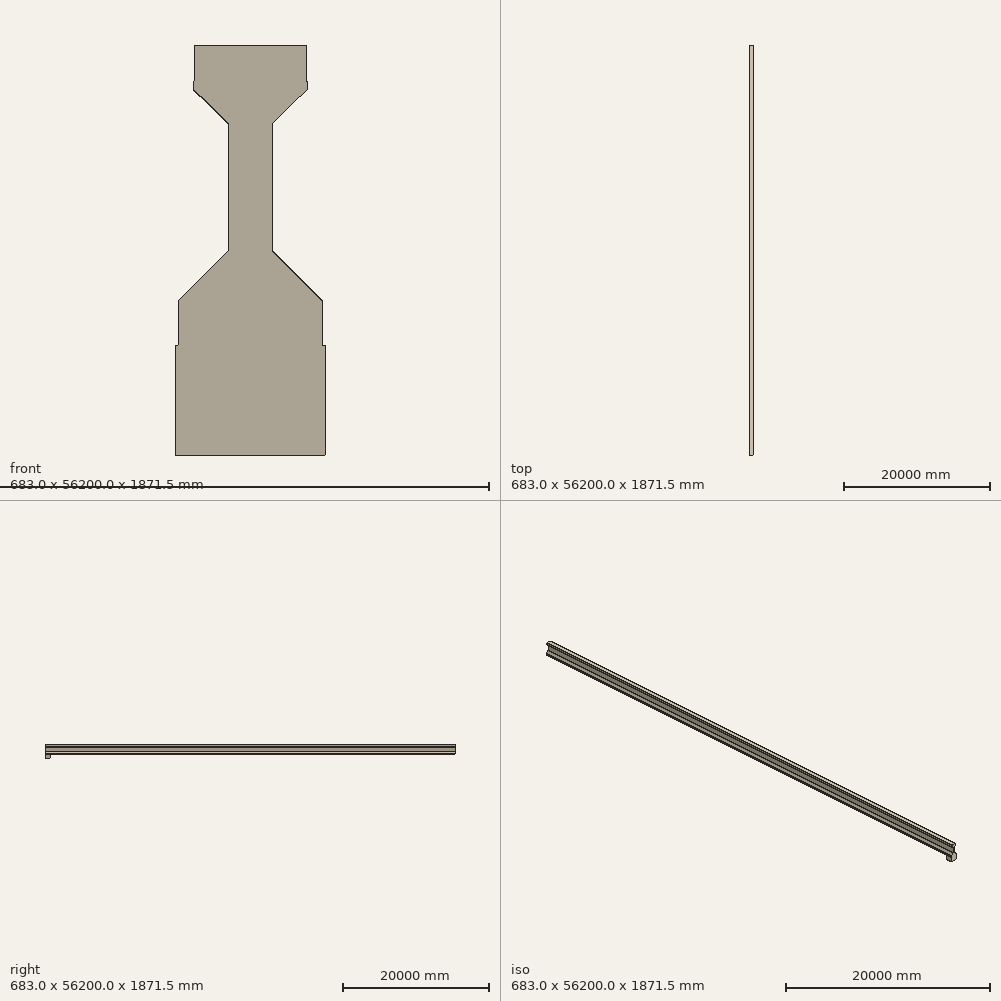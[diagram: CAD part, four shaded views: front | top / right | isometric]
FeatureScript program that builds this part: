
annotation { "Feature Type Name" : "Feature", "Feature Type Description" : "" }
export const myFeature = defineFeature(function(context is Context, id is Id, definition is map)
    precondition{}
    {
        {
            var Q0;
            Q0=qCreatedBy(makeId("Front.planeOp"),FACE);
            var sketch = newSketch(context, id + "F0", { "sketchPlane" : qUnion([Q0])});
            skLineSegment(sketch, "E0", {"start": v(0, 759.62) * mm, "end": v(-254, 759.62) * mm});
            skLineSegment(sketch, "E1", {"start": v(-254, 759.62) * mm, "end": v(-258.84, 556.48) * mm});
            skLineSegment(sketch, "E2", {"start": v(-258.84, 556.48) * mm, "end": v(-101.6, 404.08) * mm});
            skLineSegment(sketch, "E3", {"start": v(-101.6, 404.08) * mm, "end": v(-101.6, -180.12) * mm});
            skLineSegment(sketch, "E4", {"start": v(-101.6, -180.12) * mm, "end": v(-330.2, -408.72) * mm});
            skLineSegment(sketch, "E5", {"start": v(-330.2, -408.72) * mm, "end": v(-330.2, -611.92) * mm});
            skLineSegment(sketch, "E6", {"start": v(-330.2, -611.92) * mm, "end": v(0, -611.92) * mm});
            skLineSegment(sketch, "E7.MirrorCS", {"start": v(0, 759.62) * mm, "end": v(254, 759.62) * mm});
            skLineSegment(sketch, "E8.MirrorCS", {"start": v(254, 759.62) * mm, "end": v(258.84, 556.48) * mm});
            skLineSegment(sketch, "E9.MirrorCS", {"start": v(258.84, 556.48) * mm, "end": v(101.6, 404.08) * mm});
            skLineSegment(sketch, "E10.MirrorCS", {"start": v(101.6, 404.08) * mm, "end": v(101.6, -180.12) * mm});
            skLineSegment(sketch, "E11.MirrorCS", {"start": v(101.6, -180.12) * mm, "end": v(330.2, -408.72) * mm});
            skLineSegment(sketch, "E12.MirrorCS", {"start": v(330.2, -408.72) * mm, "end": v(330.2, -611.92) * mm});
            skLineSegment(sketch, "E13.MirrorCS", {"start": v(330.2, -611.92) * mm, "end": v(0, -611.92) * mm});
            skSolve(sketch);
        }
        {
            var Q0;
            Q0=makeQuery(id+"F0.imprint","IMPRINT",FACE,{"disambiguationData":[TD([[makeQuery(id+"F0.imprint","IMPRINT",EDGE,{"derivedFrom":sQuery(id+"F0.wireOp",EDGE,"E0")}),1.0]])]});
            extrude(context, id + "F1", {"entities" : qUnion([Q0]), "depth" : 56200 * mm});
        }
        {
            var Q0;
            Q0=makeQuery(id+"F1.opExtrude","SWEPT_FACE",FACE,{"disambiguationData":[OSD([sQuery(id+"F0.wireOp",EDGE,"E0"),sQuery(id+"F0.wireOp",EDGE,"E7.MirrorCS")])]});
            var sketch = newSketch(context, id + "F2", { "sketchPlane" : qUnion([Q0])});
            skLineSegment(sketch, "E14", {"start": v(-254, -56200) * mm, "end": v(0, -56200) * mm});
            skLineSegment(sketch, "E15", {"start": v(0, -56200) * mm, "end": v(0, -53450) * mm});
            skLineSegment(sketch, "E16", {"start": v(0, -56200) * mm, "end": v(254, -56200) * mm});
            skSolve(sketch);
        }
        {
            var Q0;
            Q0=makeQuery(id+"F1.opExtrude","SWEPT_FACE",FACE,{"disambiguationData":[OSD([sQuery(id+"F0.wireOp",EDGE,"E6"),sQuery(id+"F0.wireOp",EDGE,"E13.MirrorCS")])]});
            var sketch = newSketch(context, id + "F3", { "sketchPlane" : qUnion([Q0])});
            skLineSegment(sketch, "E17.bottom", {"start": v(341.5, 56200) * mm, "end": v(-341.5, 56200) * mm});
            skLineSegment(sketch, "E17.top", {"start": v(341.5, 55517) * mm, "end": v(-341.5, 55517) * mm});
            skLineSegment(sketch, "E17.left", {"start": v(341.5, 56200) * mm, "end": v(341.5, 55517) * mm});
            skLineSegment(sketch, "E17.right", {"start": v(-341.5, 56200) * mm, "end": v(-341.5, 55517) * mm});
            skPoint(sketch, "E17.middle", {"position": v(0, 55858.5) * mm});
            skPoint(sketch, "E17.middle.positionSnap0", {"position": v(0, 56200) * mm});
            skPoint(sketch, "E17.centerSnap0", {"position": v(0, 56200) * mm});
            skSolve(sketch);
        }
        {
            var Q0;
            {var subQ0=sQuery(id+"F3.wireOp",EDGE,"E17.bottom");var subQ1=makeQuery(id+"F1.opExtrude","SWEPT_EDGE",EDGE,{"disambiguationData":[OSD([sQuery(id+"F0.wireOp",EDGE,"E5"),sQuery(id+"F0.wireOp",EDGE,"E6")])]});var subQ2=makeQuery(id+"F3.imprint","INTERSECT",VERTEX,{"derivedFrom":[subQ1,subQ0]});var subQ3=makeQuery(id+"F1.opExtrude","SWEPT_EDGE",EDGE,{"disambiguationData":[OSD([sQuery(id+"F0.wireOp",EDGE,"E12.MirrorCS"),sQuery(id+"F0.wireOp",EDGE,"E13.MirrorCS")])]});var subQ4=makeQuery(id+"F3.imprint","INTERSECT",VERTEX,{"derivedFrom":[subQ3,subQ0]});Q0=makeQuery(id+"F3.imprint","IMPRINT",FACE,{"disambiguationData":[TD([[makeQuery(id+"F3.imprint","IMPRINT",EDGE,{"disambiguationData":[TD([[subQ2,-1.0],[subQ4,1.0]])],"derivedFrom":subQ0}),-1.0]])]});}
            extrude(context, id + "F4", {"entities" : qUnion([Q0]), "depth" : 500 * mm});
        }
        {
            var Q0;
            {var subQ3=sQuery(id+"F3.wireOp",EDGE,"E17.left");Q0=makeQuery(id+"F3.imprint","IMPRINT",FACE,{"disambiguationData":[TD([[makeQuery(id+"F3.imprint","IMPRINT",EDGE,{"derivedFrom":subQ3}),-1.0]])]});}
            extrude(context, id + "F5", {"entities" : qUnion([Q0]), "operationType" : NewBodyOperationType.ADD, "depth" : 500 * mm});
        }
        {
            var Q0;
            {var subQ3=sQuery(id+"F3.wireOp",EDGE,"E17.right");Q0=makeQuery(id+"F3.imprint","IMPRINT",FACE,{"disambiguationData":[TD([[makeQuery(id+"F3.imprint","IMPRINT",EDGE,{"derivedFrom":subQ3}),1.0]])]});}
            extrude(context, id + "F6", {"entities" : qUnion([Q0]), "operationType" : NewBodyOperationType.ADD, "depth" : 500 * mm});
        }
    });
